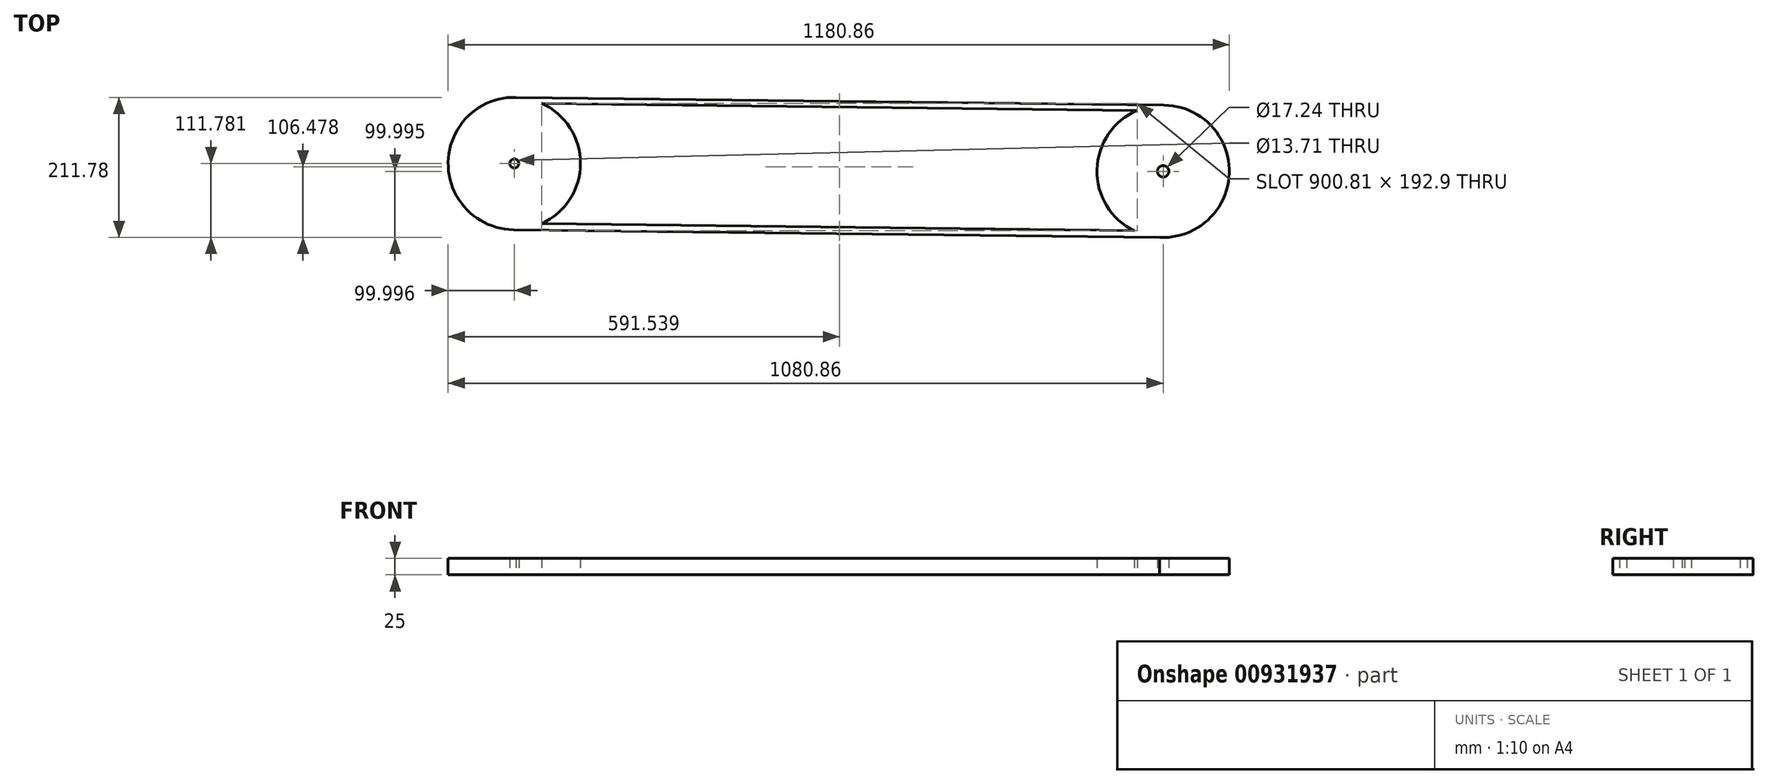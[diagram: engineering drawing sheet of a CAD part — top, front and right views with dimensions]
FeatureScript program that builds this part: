
annotation { "Feature Type Name" : "Feature", "Feature Type Description" : "" }
export const myFeature = defineFeature(function(context is Context, id is Id, definition is map)
    precondition{}
    {
        {
            var Q0;
            Q0=qCreatedBy(makeId("Top.planeOp"),FACE);
            var sketch = newSketch(context, id + "F0", { "sketchPlane" : qUnion([Q0])});
            skCircle(sketch, "E0", {"center": v(-490.6, 5.75) * mm, "radius": 100 * mm});
            skCircle(sketch, "E1", {"center": v(490.27, -6.03) * mm, "radius": 100 * mm});
            skLineSegment(sketch, "E2", {"start": v(-490.68, 105.75) * mm, "end": v(491.47, 93.96) * mm});
            skLineSegment(sketch, "E3", {"start": v(493.03, -106) * mm, "end": v(-491.79, -94.24) * mm});
            skCircle(sketch, "E4", {"center": v(-490.6, 5.75) * mm, "radius": 6.86 * mm});
            skCircle(sketch, "E5", {"center": v(490.27, -6.03) * mm, "radius": 8.62 * mm});
            skLineSegment(sketch, "E6", {"start": v(-449.26, -85.3) * mm, "end": v(446.62, -96) * mm});
            skLineSegment(sketch, "E7", {"start": v(451.35, 86.08) * mm, "end": v(-449.45, 96.9) * mm});
            skSolve(sketch);
        }
        {
            var Q0;
            Q0 = qSketchRegion(id + "F0", true);
            extrude(context, id + "F1", {"entities" : qUnion([Q0]), "depth" : 25 * mm, "offsetDistance" : 25 * mm});
        }
    });
